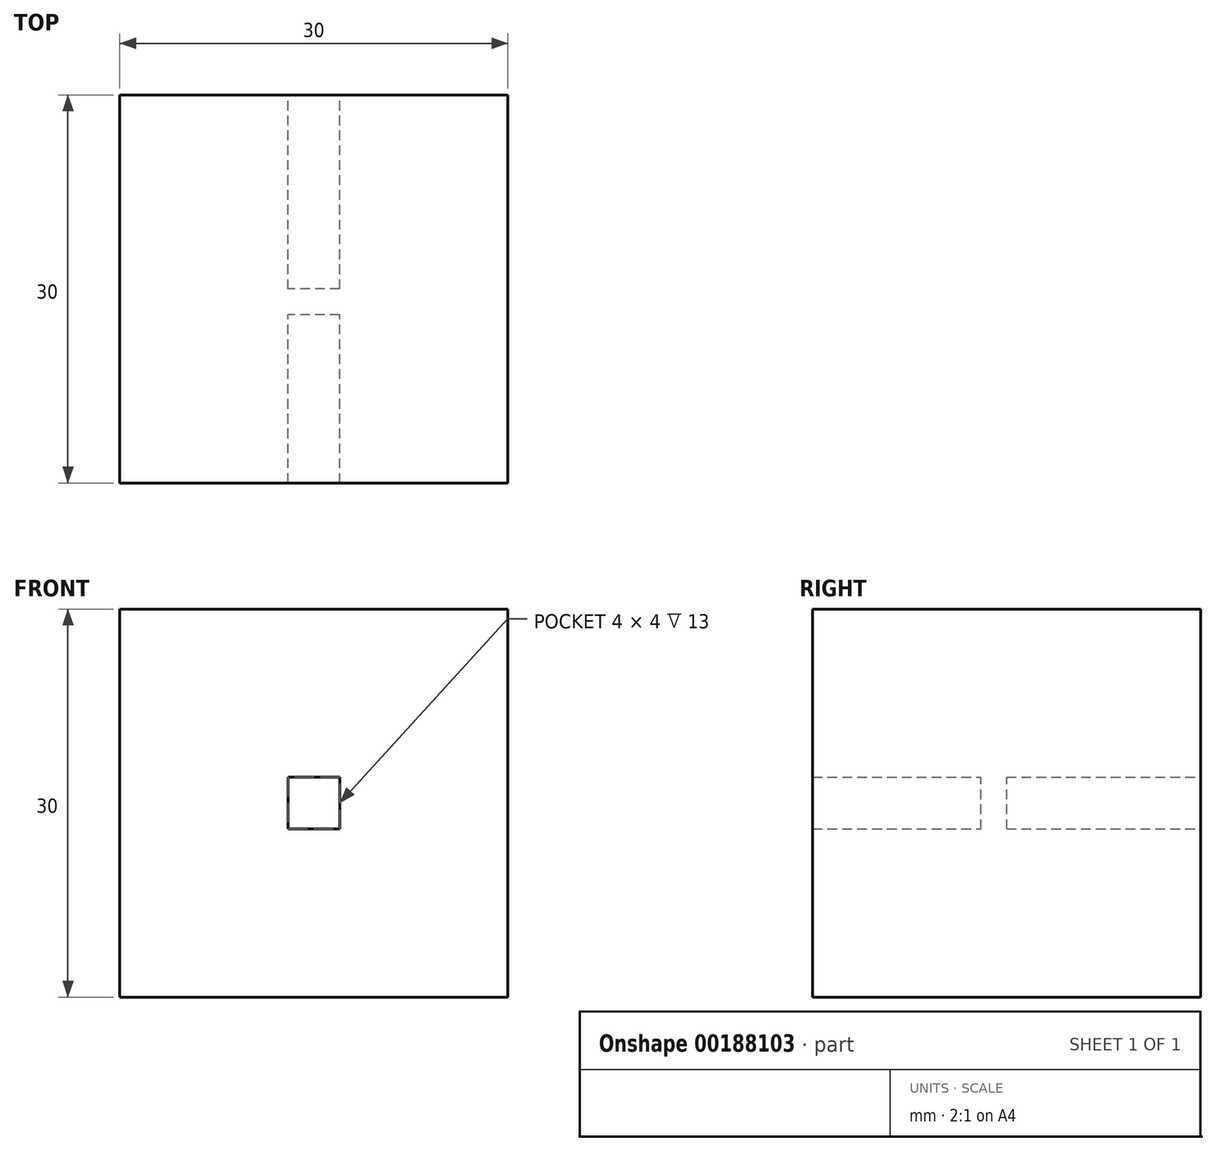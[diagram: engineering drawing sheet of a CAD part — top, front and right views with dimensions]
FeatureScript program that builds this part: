
annotation { "Feature Type Name" : "Feature", "Feature Type Description" : "" }
export const myFeature = defineFeature(function(context is Context, id is Id, definition is map)
    precondition{}
    {
        {
            var Q0;
            Q0=qCreatedBy(makeId("Front.planeOp"),FACE);
            var sketch = newSketch(context, id + "F0", { "sketchPlane" : qUnion([Q0])});
            skLineSegment(sketch, "E0.bottom", {"start": v(15, -15) * mm, "end": v(-15, -15) * mm});
            skLineSegment(sketch, "E0.top", {"start": v(15, 15) * mm, "end": v(-15, 15) * mm});
            skLineSegment(sketch, "E0.left", {"start": v(15, -15) * mm, "end": v(15, 15) * mm});
            skLineSegment(sketch, "E0.right", {"start": v(-15, -15) * mm, "end": v(-15, 15) * mm});
            skPoint(sketch, "E0.middle", {"position": v(0, 0) * mm});
            skLineSegment(sketch, "E1.bottom", {"start": v(2, -2) * mm, "end": v(-2, -2) * mm});
            skLineSegment(sketch, "E1.top", {"start": v(2, 2) * mm, "end": v(-2, 2) * mm});
            skLineSegment(sketch, "E1.left", {"start": v(2, -2) * mm, "end": v(2, 2) * mm});
            skLineSegment(sketch, "E1.right", {"start": v(-2, -2) * mm, "end": v(-2, 2) * mm});
            skSolve(sketch);
        }
        {
            var Q0;
            Q0 = qSketchRegion(id + "F0", true);
            extrude(context, id + "F1", {"entities" : qUnion([Q0]), "endBound" : BoundingType.SYMMETRIC, "depth" : 30 * mm});
        }
        {
            var Q0;
            Q0=makeQuery(id+"F0.imprint","IMPRINT",FACE,{"disambiguationData":[TD([[makeQuery(id+"F0.imprint","IMPRINT",EDGE,{"derivedFrom":sQuery(id+"F0.wireOp",EDGE,"E1.bottom")}),-1.0]])]});
            extrude(context, id + "F2", {"entities" : qUnion([Q0]), "operationType" : NewBodyOperationType.ADD, "depth" : 2 * mm});
        }
    });
